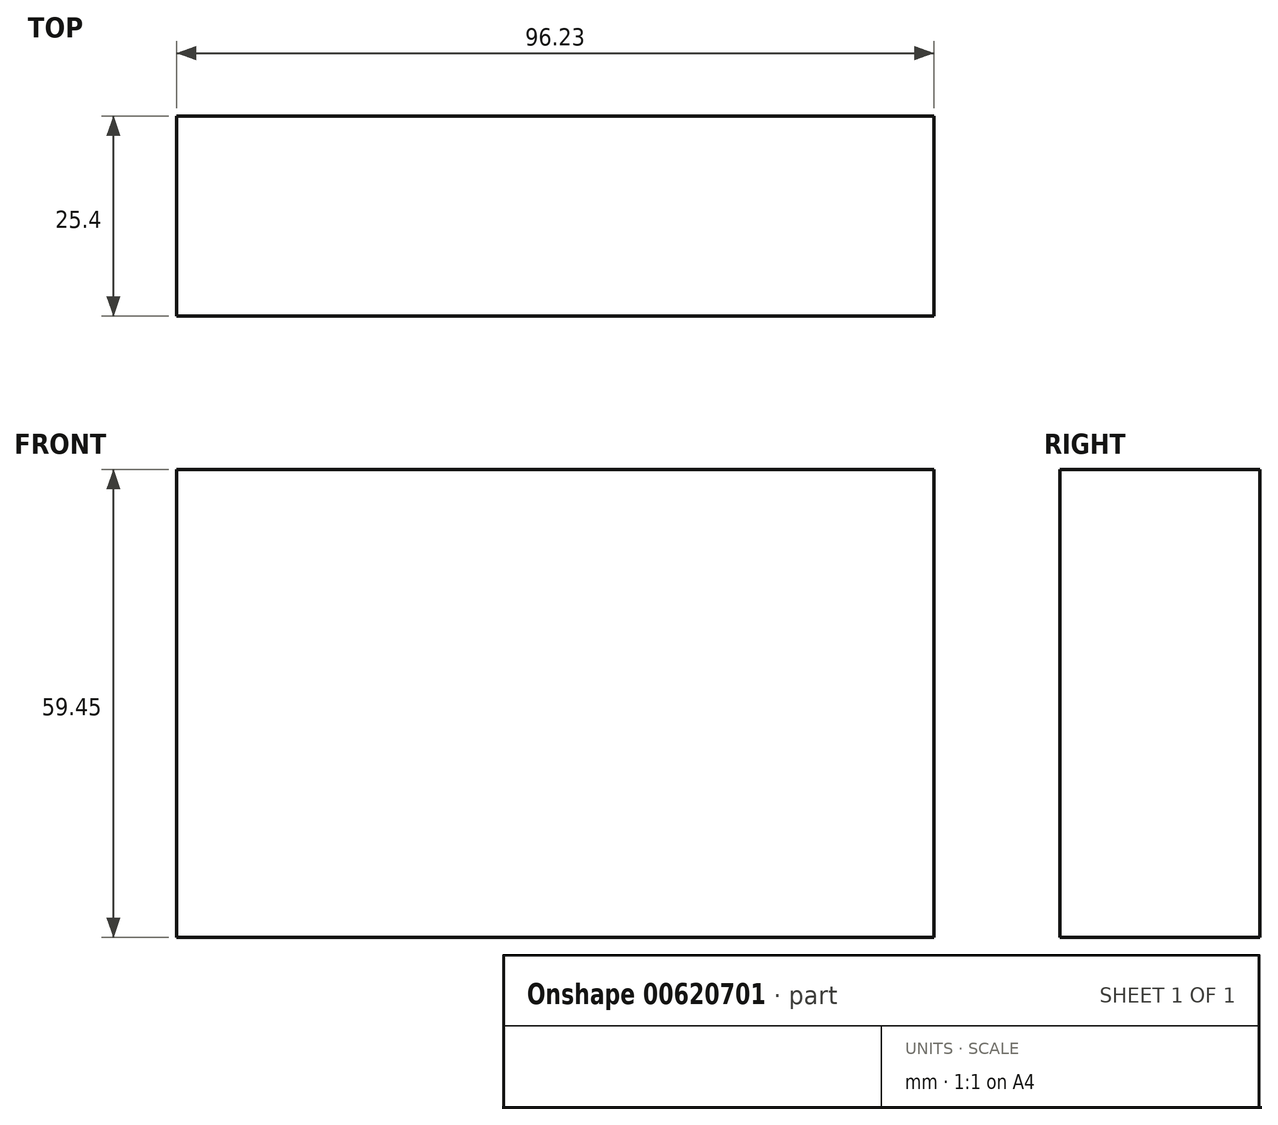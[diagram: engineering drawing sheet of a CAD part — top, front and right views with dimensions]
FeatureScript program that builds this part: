
annotation { "Feature Type Name" : "Feature", "Feature Type Description" : "" }
export const myFeature = defineFeature(function(context is Context, id is Id, definition is map)
    precondition{}
    {
        {
            var Q0;
            Q0=qCreatedBy(makeId("Front.planeOp"),FACE);
            var sketch = newSketch(context, id + "F0", { "sketchPlane" : qUnion([Q0])});
            skLineSegment(sketch, "E0.bottom", {"start": v(-43.72, 0) * mm, "end": v(52.5, 0) * mm});
            skLineSegment(sketch, "E0.top", {"start": v(-43.72, -59.45) * mm, "end": v(52.5, -59.45) * mm});
            skLineSegment(sketch, "E0.left", {"start": v(-43.72, 0) * mm, "end": v(-43.72, -59.45) * mm});
            skLineSegment(sketch, "E0.right", {"start": v(52.5, 0) * mm, "end": v(52.5, -59.45) * mm});
            skLineSegment(sketch, "E1.bottom", {"start": v(52.5, -29.72) * mm, "end": v(90, -29.72) * mm, "construction": true});
            skLineSegment(sketch, "E1.top", {"start": v(52.5, 0) * mm, "end": v(90, 0) * mm, "construction": true});
            skLineSegment(sketch, "E1.left", {"start": v(52.5, -29.72) * mm, "end": v(52.5, 0) * mm, "construction": true});
            skLineSegment(sketch, "E1.right", {"start": v(90, -29.72) * mm, "end": v(90, 0) * mm, "construction": true});
            skLineSegment(sketch, "E2.bottom", {"start": v(91.22, 94.36) * mm, "end": v(97.8, 94.36) * mm, "construction": true});
            skLineSegment(sketch, "E2.top", {"start": v(91.22, -10.98) * mm, "end": v(97.8, -10.98) * mm, "construction": true});
            skLineSegment(sketch, "E2.left", {"start": v(91.22, 94.36) * mm, "end": v(91.22, -10.98) * mm, "construction": true});
            skLineSegment(sketch, "E2.right", {"start": v(97.8, 94.36) * mm, "end": v(97.8, -10.98) * mm, "construction": true});
            skLineSegment(sketch, "E3.bottom", {"start": v(-41.58, -33.26) * mm, "end": v(10.02, -33.26) * mm, "construction": true});
            skLineSegment(sketch, "E3.top", {"start": v(-41.58, 84.56) * mm, "end": v(10.02, 84.56) * mm, "construction": true});
            skLineSegment(sketch, "E3.left", {"start": v(-41.58, -33.26) * mm, "end": v(-41.58, 84.56) * mm, "construction": true});
            skLineSegment(sketch, "E3.right", {"start": v(10.02, -33.26) * mm, "end": v(10.02, 84.56) * mm, "construction": true});
            skSolve(sketch);
        }
        {
            var Q0;
            Q0=makeQuery(id+"F0.imprint","IMPRINT",FACE,{"disambiguationData":[TD([[makeQuery(id+"F0.imprint","IMPRINT",EDGE,{"derivedFrom":sQuery(id+"F0.wireOp",EDGE,"E0.bottom")}),-1.0]])]});
            extrude(context, id + "F1", {"entities" : qUnion([Q0]), "depth" : 25.4 * mm, "offsetDistance" : 25.4 * mm});
        }
    });
